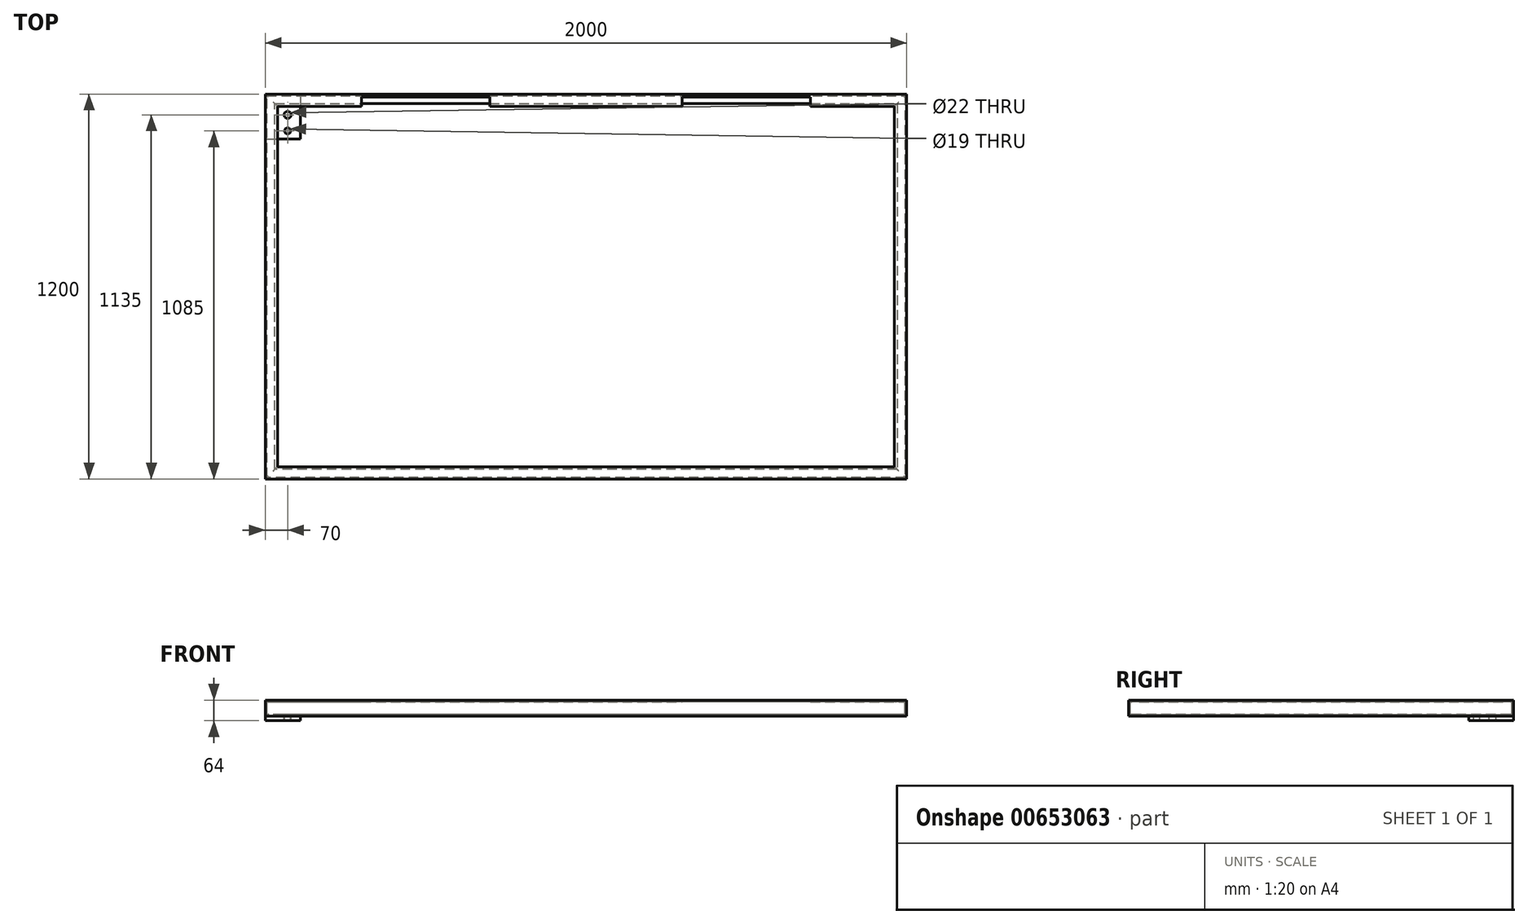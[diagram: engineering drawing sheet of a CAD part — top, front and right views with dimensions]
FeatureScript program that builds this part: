
annotation { "Feature Type Name" : "Feature", "Feature Type Description" : "" }
export const myFeature = defineFeature(function(context is Context, id is Id, definition is map)
    precondition{}
    {
        {
            var Q0;
            Q0=qCreatedBy(makeId("Front.planeOp"),FACE);
            var sketch = newSketch(context, id + "F0", { "sketchPlane" : qUnion([Q0])});
            skLineSegment(sketch, "E0.bottom", {"start": v(0, 0) * mm, "end": v(30, 0) * mm});
            skLineSegment(sketch, "E0.top", {"start": v(0, 50) * mm, "end": v(38, 50) * mm});
            skLineSegment(sketch, "E0.left", {"start": v(0, 0) * mm, "end": v(0, 50) * mm});
            skLineSegment(sketch, "E1.0", {"start": v(10, 45) * mm, "end": v(33, 45) * mm});
            skLineSegment(sketch, "E1.1", {"start": v(5, 10) * mm, "end": v(5, 40) * mm});
            skLineSegment(sketch, "E1.2", {"start": v(10, 5) * mm, "end": v(25, 5) * mm});
            skLineSegment(sketch, "E2", {"start": v(38, 50) * mm, "end": v(38, 50) * mm});
            skLineSegment(sketch, "E3", {"start": v(30, 0) * mm, "end": v(30, 0) * mm});
            skPoint(sketch, "E4.visualSharp", {"position": v(38, 45) * mm});
            skArc(sketch, "E4.filletArc", {"start": v(33, 45) * mm, "mid": v(36.54, 46.46) * mm, "end": v(38, 50) * mm});
            skPoint(sketch, "E5.visualSharp", {"position": v(30, 5) * mm});
            skArc(sketch, "E5.filletArc", {"start": v(30, 0) * mm, "mid": v(28.54, 3.54) * mm, "end": v(25, 5) * mm});
            skPoint(sketch, "E6.visualSharp", {"position": v(5, 5) * mm});
            skArc(sketch, "E6.filletArc", {"start": v(5, 10) * mm, "mid": v(6.46, 6.46) * mm, "end": v(10, 5) * mm});
            skPoint(sketch, "E7.visualSharp", {"position": v(5, 45) * mm});
            skArc(sketch, "E7.filletArc", {"start": v(10, 45) * mm, "mid": v(6.46, 43.54) * mm, "end": v(5, 40) * mm});
            skSolve(sketch);
        }
        {
            var Q0;
            Q0=qCreatedBy(makeId("Top.planeOp"),FACE);
            var sketch = newSketch(context, id + "F1", { "sketchPlane" : qUnion([Q0])});
            skLineSegment(sketch, "E8.bottom", {"start": v(0, 0) * mm, "end": v(2000, 0) * mm});
            skLineSegment(sketch, "E8.top", {"start": v(0, 1200) * mm, "end": v(2000, 1200) * mm});
            skLineSegment(sketch, "E8.left", {"start": v(0, 0) * mm, "end": v(0, 1200) * mm});
            skLineSegment(sketch, "E8.right", {"start": v(2000, 0) * mm, "end": v(2000, 1200) * mm});
            skLineSegment(sketch, "E9", {"start": v(1000, 0) * mm, "end": v(1000, 1200) * mm, "construction": true});
            skLineSegment(sketch, "E10", {"start": v(2000, 600) * mm, "end": v(0, 600) * mm, "construction": true});
            skSolve(sketch);
        }
        {
            var Q0;
            Q0 = qSketchRegion(id + "F0", true);
            var Q1;
            Q1 = qConstructionFilter(qBodyType(qCreatedBy(id + "F1" ,EDGE), BodyType.WIRE), ConstructionObject.NO);
            sweep(context, id + "F2", {"profiles" : qUnion([Q0]), "path" : qUnion([Q1])});
        }
        {
            var Q0;
            Q0=qCreatedBy(makeId("Top.planeOp"),FACE);
            var sketch = newSketch(context, id + "F3", { "sketchPlane" : qUnion([Q0])});
            skLineSegment(sketch, "E11.bottom", {"start": v(0, 1200) * mm, "end": v(110, 1200) * mm});
            skLineSegment(sketch, "E11.top", {"start": v(0, 1060) * mm, "end": v(110, 1060) * mm});
            skLineSegment(sketch, "E11.left", {"start": v(0, 1200) * mm, "end": v(0, 1060) * mm});
            skLineSegment(sketch, "E11.right", {"start": v(110, 1200) * mm, "end": v(110, 1060) * mm});
            skLineSegment(sketch, "E12.0", {"start": v(0, 0) * mm, "end": v(0, 1200) * mm});
            skLineSegment(sketch, "E13.0.0", {"start": v(2000, 1200) * mm, "end": v(0, 1200) * mm, "construction": true});
            skLineSegment(sketch, "E13.0.1", {"start": v(0, 1200) * mm, "end": v(0, 0) * mm, "construction": true});
            skLineSegment(sketch, "E13.0.2", {"start": v(0, 0) * mm, "end": v(2000, 0) * mm, "construction": true});
            skLineSegment(sketch, "E13.0.3", {"start": v(2000, 0) * mm, "end": v(2000, 1200) * mm, "construction": true});
            skPoint(sketch, "E14", {"position": v(70, 1135) * mm});
            skPoint(sketch, "E15", {"position": v(70, 1085) * mm});
            skLineSegment(sketch, "E16", {"start": v(70, 1200) * mm, "end": v(70, 1060) * mm, "construction": true});
            skSolve(sketch);
        }
        {
            var Q0;
            Q0 = qSketchRegion(id + "F3", true);
            extrude(context, id + "F4", {"entities" : qUnion([Q0]), "operationType" : NewBodyOperationType.ADD, "oppositeDirection" : true, "depth" : 14 * mm, "offsetDistance" : 25 * mm});
        }
        {
            var Q0;
            Q0=sQuery(id+"F3.wireOp",VERTEX,"E14");
            var Q1;
            Q1=makeQuery(id+"F2.opSweep","SWEPT_BODY",BODY,{"disambiguationData":[OSD([sQuery(id+"F0.wireOp",EDGE,"E0.bottom"),sQuery(id+"F0.wireOp",EDGE,"E0.top"),sQuery(id+"F0.wireOp",EDGE,"E0.left"),sQuery(id+"F0.wireOp",EDGE,"E1.0"),sQuery(id+"F0.wireOp",EDGE,"E1.1"),sQuery(id+"F0.wireOp",EDGE,"E1.2"),sQuery(id+"F0.wireOp",EDGE,"E4.filletArc"),sQuery(id+"F0.wireOp",EDGE,"E5.filletArc"),sQuery(id+"F0.wireOp",EDGE,"E6.filletArc"),sQuery(id+"F0.wireOp",EDGE,"E7.filletArc"),sQuery(id+"F1.wireOp",EDGE,"E8.right")])]});
            hole(context, id + "F5", {"style" : HoleStyle.SIMPLE, "endStyle" : HoleEndStyle.THROUGH, "standardTappedOrClearance" : lookupTablePath({ "standard" : "ISO", "fit" : "Normal", "size" : "M20", "type" : "Clearance" }), "standardBlindInLast" : lookupTablePath({ "fit" : "Standard", "standard" : "ISO", "size" : "M20", "type" : "Clearance" }), "holeDiameter" : 22 * mm, "majorDiameter" : 5 * mm, "isTappedThrough" : true, "tappedDepth" : 12 * mm, "tapClearance" : 3, "locations" : qUnion([Q0]), "scope" : qUnion([Q1])});
        }
        {
            var Q0;
            Q0=sQuery(id+"F3.wireOp",VERTEX,"E15");
            var Q1;
            Q1=makeQuery(id+"F2.opSweep","SWEPT_BODY",BODY,{"disambiguationData":[OSD([sQuery(id+"F0.wireOp",EDGE,"E0.bottom"),sQuery(id+"F0.wireOp",EDGE,"E0.top"),sQuery(id+"F0.wireOp",EDGE,"E0.left"),sQuery(id+"F0.wireOp",EDGE,"E1.0"),sQuery(id+"F0.wireOp",EDGE,"E1.1"),sQuery(id+"F0.wireOp",EDGE,"E1.2"),sQuery(id+"F0.wireOp",EDGE,"E4.filletArc"),sQuery(id+"F0.wireOp",EDGE,"E5.filletArc"),sQuery(id+"F0.wireOp",EDGE,"E6.filletArc"),sQuery(id+"F0.wireOp",EDGE,"E7.filletArc"),sQuery(id+"F1.wireOp",EDGE,"E8.right")])]});
            hole(context, id + "F6", {"style" : HoleStyle.SIMPLE, "endStyle" : HoleEndStyle.THROUGH, "holeDiameter" : 19 * mm, "majorDiameter" : 5 * mm, "isTappedThrough" : true, "tappedDepth" : 12 * mm, "tapClearance" : 3, "locations" : qUnion([Q0]), "scope" : qUnion([Q1])});
        }
        {
            var Q0;
            Q0=sQuery(id+"F1.wireOp",EDGE,"E9");
            cPlane(context, id + "F7", {"entities" : qUnion([Q0]), "cplaneType" : CPlaneType.MID_PLANE, "offset" : 25 * mm, "width" : 150 * mm, "height" : 150 * mm});
        }
        {
            var Q0;
            Q0=sQuery(id+"F1.wireOp",EDGE,"E10");
            cPlane(context, id + "F8", {"entities" : qUnion([Q0]), "cplaneType" : CPlaneType.MID_PLANE, "offset" : 25 * mm, "width" : 150 * mm, "height" : 150 * mm});
        }
        {
            var Q0;
            Q0=makeQuery(id+"F2.opSweep","SWEPT_FACE",FACE,{"disambiguationData":[OSD([sQuery(id+"F0.wireOp",EDGE,"E0.top"),sQuery(id+"F1.wireOp",EDGE,"E8.left")])]});
            var sketch = newSketch(context, id + "F9", { "sketchPlane" : qUnion([Q0])});
            skLineSegment(sketch, "E17.bottom", {"start": v(700, 1140) * mm, "end": v(300, 1140) * mm});
            skLineSegment(sketch, "E17.top", {"start": v(700, 1190) * mm, "end": v(300, 1190) * mm});
            skLineSegment(sketch, "E17.left", {"start": v(700, 1140) * mm, "end": v(700, 1190) * mm});
            skLineSegment(sketch, "E17.right", {"start": v(300, 1140) * mm, "end": v(300, 1190) * mm});
            skLineSegment(sketch, "E18.MirrorCS", {"start": v(1300, 1190) * mm, "end": v(1700, 1190) * mm});
            skLineSegment(sketch, "E19.MirrorCS", {"start": v(1300, 1140) * mm, "end": v(1700, 1140) * mm});
            skLineSegment(sketch, "E20.MirrorCS", {"start": v(1700, 1140) * mm, "end": v(1700, 1190) * mm});
            skLineSegment(sketch, "E21.MirrorCS", {"start": v(1300, 1140) * mm, "end": v(1300, 1190) * mm});
            skSolve(sketch);
        }
        {
            var Q0;
            Q0 = qSketchRegion(id + "F9", true);
            extrude(context, id + "F10", {"entities" : qUnion([Q0]), "operationType" : NewBodyOperationType.REMOVE, "oppositeDirection" : true, "depth" : 10 * mm, "offsetDistance" : 25 * mm});
        }
    });
